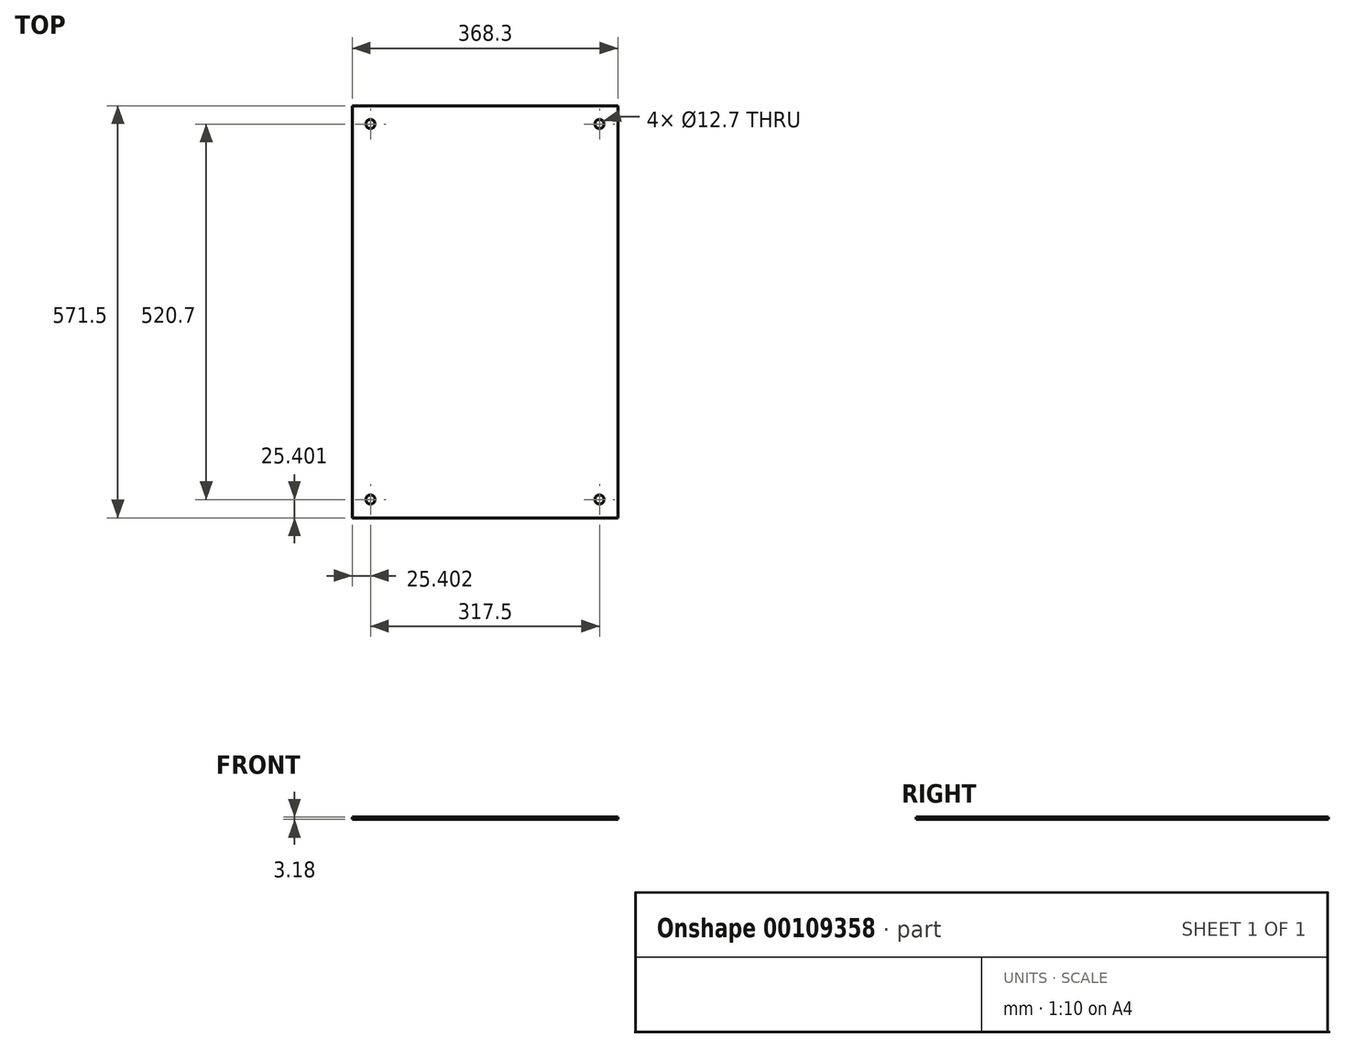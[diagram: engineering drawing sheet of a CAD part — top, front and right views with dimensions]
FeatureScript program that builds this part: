
annotation { "Feature Type Name" : "Feature", "Feature Type Description" : "" }
export const myFeature = defineFeature(function(context is Context, id is Id, definition is map)
    precondition{}
    {
        {
            var Q0;
            Q0=qCreatedBy(makeId("Top.planeOp"),FACE);
            var sketch = newSketch(context, id + "F0", { "sketchPlane" : qUnion([Q0])});
            skLineSegment(sketch, "E0.bottom", {"start": v(-170.9, 308.57) * mm, "end": v(197.4, 308.57) * mm});
            skLineSegment(sketch, "E0.top", {"start": v(-170.9, -262.93) * mm, "end": v(197.4, -262.93) * mm});
            skLineSegment(sketch, "E0.left", {"start": v(-170.9, 308.57) * mm, "end": v(-170.9, -262.93) * mm});
            skLineSegment(sketch, "E0.right", {"start": v(197.4, 308.57) * mm, "end": v(197.4, -262.93) * mm});
            skSolve(sketch);
        }
        {
            var Q0;
            Q0=makeQuery(id+"F0.imprint","IMPRINT",FACE,{"disambiguationData":[TD([[makeQuery(id+"F0.imprint","IMPRINT",EDGE,{"derivedFrom":sQuery(id+"F0.wireOp",EDGE,"E0.bottom")}),-1.0]])]});
            extrude(context, id + "F1", {"entities" : qUnion([Q0]), "endBound" : BoundingType.SYMMETRIC, "depth" : 3.17 * mm});
        }
        {
            var Q0;
            Q0=makeQuery(id+"F1.opExtrude","CAP_FACE",FACE,{"disambiguationData":[OSD([sQuery(id+"F0.wireOp",EDGE,"E0.bottom"),sQuery(id+"F0.wireOp",EDGE,"E0.top"),sQuery(id+"F0.wireOp",EDGE,"E0.left"),sQuery(id+"F0.wireOp",EDGE,"E0.right")])],"isStart":false});
            var sketch = newSketch(context, id + "F2", { "sketchPlane" : qUnion([Q0])});
            skCircle(sketch, "E1", {"center": v(172, 283.17) * mm, "radius": 6.35 * mm});
            skCircle(sketch, "E2.MirrorC", {"center": v(-145.5, 283.17) * mm, "radius": 6.35 * mm});
            skCircle(sketch, "E3.MirrorC", {"center": v(-145.5, -237.53) * mm, "radius": 6.35 * mm});
            skCircle(sketch, "E4.MirrorC", {"center": v(172, -237.53) * mm, "radius": 6.35 * mm});
            skSolve(sketch);
        }
        {
            var Q0;
            Q0 = qSketchRegion(id + "F2", true);
            extrude(context, id + "F3", {"entities" : qUnion([Q0]), "operationType" : NewBodyOperationType.REMOVE, "oppositeDirection" : true, "depth" : 25.4 * mm});
        }
    });
